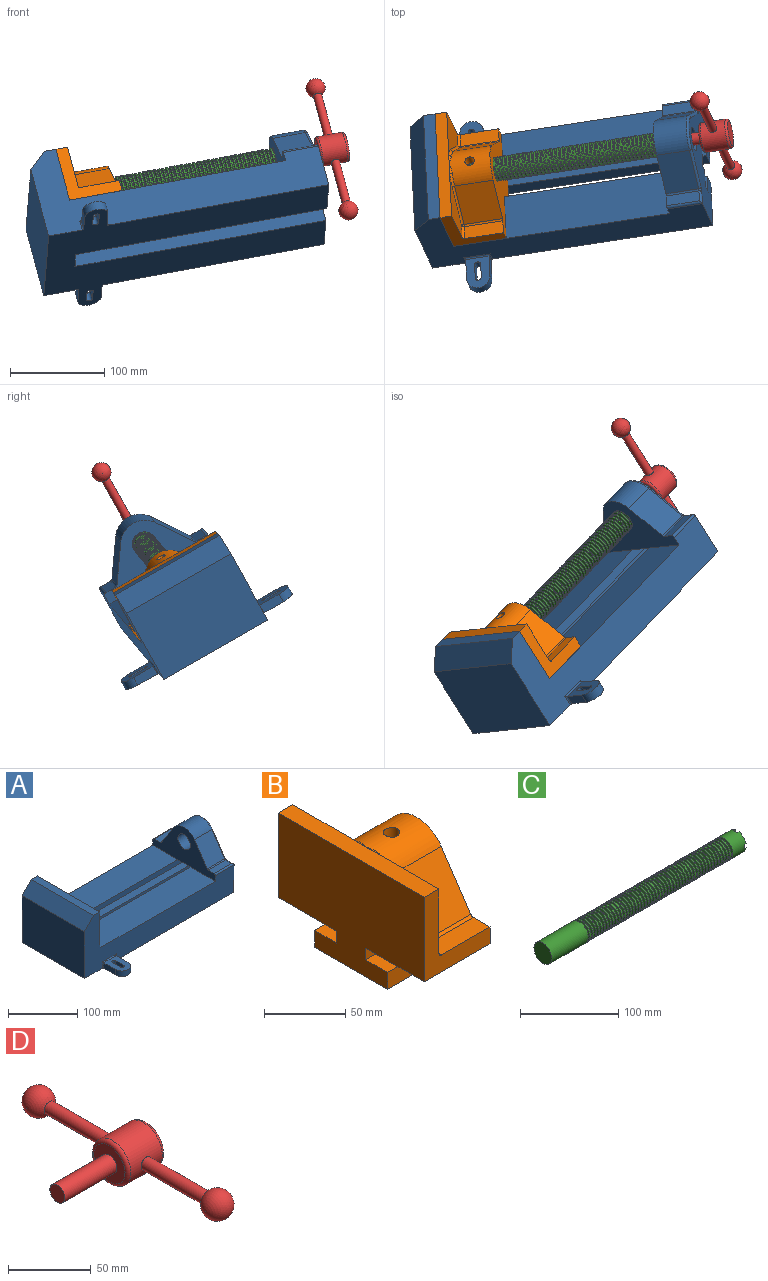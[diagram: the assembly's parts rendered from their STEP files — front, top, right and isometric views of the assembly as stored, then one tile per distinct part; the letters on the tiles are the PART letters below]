
ASSEMBLY  parts=4 mates=6
PART A: 61 faces, bbox 304.8x203.2x103.7 mm
  f0: plane 304.8x101.6mm, normal (0,1,0), area 13520.3mm2, adj f3,f4,f5,f6,f7,f8,f9,f16
  f1: plane 304.8x101.6mm, normal (0,-1,0), area 13520.3mm2, adj f2,f3,f5,f6,f7,f8,f9,f16
  f2: plane 234.95x50.8mm, normal (0,0,1), area 11935.5mm2, adj f1,f5,f16,f26
  f3: plane 127x99.06mm, normal (1,0,0), area 7097.5mm2, adj f0,f1,f9,f14,f17,f18,f19,f20
  f4: plane 234.95x50.8mm, normal (0,0,1), area 11935.5mm2, adj f0,f5,f16,f27
  f5: plane 127x101.6mm, normal (1,0,0), area 9516.1mm2, adj f0,f1,f2,f4,f6,f9,f18,f19
  f6: plane 127x12.7mm, normal (0,0,1), area 1612.9mm2, adj f0,f1,f5,f7
  f7: plane 127x19.05mm, normal (-0.71,0,0.71), area 3421.5mm2, adj f0,f1,f6,f8
  f8: plane 127x82.55mm, normal (-1,0,0), area 10483.8mm2, adj f0,f1,f7,f9
  f9: plane 304.8x203.2mm, normal (0,0,-1), area 33298.3mm2, adj f0,f1,f3,f5,f8,f21,f22,f39
  f10: plane 35.56x11.98mm, normal (0,0,1), area 426mm2, adj f16,f28,f29,f30
  f11: plane 38.43x35.56mm, normal (0,0.83,0.56), area 1645.4mm2, adj f12,f16,f29,f32
  f12: cylinder r=25.4mm len=42.19mm, axis (1,0,0), area 1770.2mm2, adj f11,f13,f16,f33
  f13: plane 38.43x35.56mm, normal (0,-0.83,0.56), area 1645.4mm2, adj f12,f16,f34,f35
  f14: cylinder r=12.7mm len=38.1mm, axis (1,0,0), area 3040.2mm2, adj f3,f16
  f15: plane 35.56x11.98mm, normal (0,0,1), area 426mm2, adj f16,f34,f36,f38
  f16: plane 127x63.5mm, normal (-1,0,0), area 4155.5mm2, adj f0,f1,f2,f4,f10,f11,f12,f13
  f17: plane 38.1x25.4mm, normal (0,0,-1), area 967.7mm2, adj f3,f16,f26,f27
  f18: plane 273.05x19.05mm, normal (0,0,-1), area 5201.6mm2, adj f3,f5,f19,f26
  f19: plane 273.05x12.7mm, normal (0,1,0), area 3467.7mm2, adj f3,f5,f18,f20
  f20: plane 273.05x19.05mm, normal (0,0,1), area 5201.6mm2, adj f3,f5,f19,f21
  f21: plane 273.05x16.51mm, normal (0,1,0), area 4508.1mm2, adj f3,f5,f9,f20
  f22: plane 273.05x16.51mm, normal (0,-1,0), area 4508.1mm2, adj f3,f5,f9,f23
  f23: plane 273.05x19.05mm, normal (0,0,1), area 5201.6mm2, adj f3,f5,f22,f24
  f24: plane 273.05x12.7mm, normal (0,-1,0), area 3467.7mm2, adj f3,f5,f23,f25
  f25: plane 273.05x19.05mm, normal (0,0,-1), area 5201.6mm2, adj f3,f5,f24,f27
  f26: plane 273.05x8.89mm, normal (0,1,0), area 2427.4mm2, adj f2,f3,f5,f17,f18
  f27: plane 273.05x8.89mm, normal (0,-1,0), area 2427.4mm2, adj f3,f4,f5,f17,f25
  f28: cylinder r=2.54mm len=38.1mm, axis (1,0,0), area 148.3mm2, adj f0,f10,f16,f30
  f29: cylinder r=2.54mm len=35.56mm, axis (-1,0,0), area 88.5mm2, adj f10,f11,f16,f31
  f30: cylinder r=2.54mm len=14.52mm, axis (0,1,0), area 54.3mm2, adj f3,f10,f28,f31
  f31: torus R=5.08mm, axis (-1,0,0), area 13.5mm2, adj f3,f29,f30,f32
  f32: cylinder r=2.54mm len=39.84mm, axis (0,0.56,-0.83), area 184.6mm2, adj f3,f11,f31,f33
  f33: torus R=22.86mm, axis (-1,0,0), area 191.4mm2, adj f3,f12,f32,f35
  f34: cylinder r=2.54mm len=35.56mm, axis (-1,0,0), area 88.5mm2, adj f13,f15,f16,f37
  f35: cylinder r=2.54mm len=39.84mm, axis (0,0.56,0.83), area 184.6mm2, adj f3,f13,f33,f37
  f36: cylinder r=2.54mm len=38.1mm, axis (-1,0,0), area 148.3mm2, adj f1,f15,f16,f38
  f37: torus R=5.08mm, axis (-1,0,0), area 13.5mm2, adj f3,f34,f35,f38
  f38: cylinder r=2.54mm len=14.52mm, axis (0,1,0), area 54.3mm2, adj f3,f15,f36,f37
  f39: plane 23.88x9.53mm, normal (-1,0,0), area 227.4mm2, adj f9,f45,f46,f60
  f40: plane 23.88x9.53mm, normal (1,0,0), area 227.4mm2, adj f9,f45,f46,f58
  f41: cylinder r=3.3mm len=9.53mm, axis (0,0,-1), area 98.8mm2, adj f9,f42,f44,f46
  f42: plane 15.62x9.53mm, normal (-1,0,0), area 148.8mm2, adj f9,f41,f43,f46
  f43: cylinder r=3.3mm len=9.53mm, axis (0,0,-1), area 98.8mm2, adj f9,f42,f44,f46
  f44: plane 15.62x9.53mm, normal (1,0,0), area 148.8mm2, adj f9,f41,f43,f46
  f45: cylinder r=12.7mm len=25.4mm, axis (0,0,-1), area 380mm2, adj f9,f39,f40,f46
  f46: plane 36.58x25.4mm, normal (0,0,1), area 722.4mm2, adj f39,f40,f41,f42,f43,f44,f45,f59
  f47: plane 23.88x9.53mm, normal (-1,0,0), area 227.4mm2, adj f9,f53,f54,f56
  f48: plane 23.88x9.53mm, normal (1,0,0), area 227.4mm2, adj f9,f53,f54,f55
  f49: cylinder r=3.3mm len=9.53mm, axis (0,0,-1), area 98.8mm2, adj f9,f50,f52,f54
  f50: plane 15.62x9.53mm, normal (-1,0,0), area 148.8mm2, adj f9,f49,f51,f54
  f51: cylinder r=3.3mm len=9.53mm, axis (0,0,-1), area 98.8mm2, adj f9,f50,f52,f54
  f52: plane 15.62x9.53mm, normal (1,0,0), area 148.8mm2, adj f9,f49,f51,f54
  f53: cylinder r=12.7mm len=25.4mm, axis (0,0,-1), area 380mm2, adj f9,f47,f48,f54
  f54: plane 36.58x25.4mm, normal (0,0,1), area 722.4mm2, adj f47,f48,f49,f50,f51,f52,f53,f57
  f55: cylinder r=1.52mm len=11.05mm, axis (0,0,-1), area 24.1mm2, adj f0,f9,f48,f57
  f56: cylinder r=1.52mm len=11.05mm, axis (0,0,1), area 24.1mm2, adj f0,f9,f47,f57
  f57: cylinder r=1.52mm len=28.45mm, axis (1,0,0), area 63.5mm2, adj f0,f54,f55,f56
  f58: cylinder r=1.52mm len=11.05mm, axis (0,0,1), area 24.1mm2, adj f1,f9,f40,f59
  f59: cylinder r=1.52mm len=28.45mm, axis (-1,0,0), area 63.5mm2, adj f1,f46,f58,f60
  f60: cylinder r=1.52mm len=11.05mm, axis (0,0,-1), area 24.1mm2, adj f1,f9,f39,f59
PART B: 36 faces, bbox 57.2x127x89 mm
  f0: plane 57.15x50.8mm, normal (0,0,-1), area 2903.2mm2, adj f6,f9,f10,f23
  f1: cylinder r=12.7mm len=44.45mm, axis (1,0,0), area 3464.3mm2, adj f6,f15,f16
  f2: plane 41.91x14.52mm, normal (0,0,1), area 608.5mm2, adj f6,f11,f24,f25
  f3: plane 51.86x48.26mm, normal (1,0,0), area 1495.7mm2, adj f8,f10,f31,f33,f35
  f4: plane 51.86x48.26mm, normal (1,0,0), area 1495.7mm2, adj f8,f11,f24,f28,f29
  f5: plane 57.15x50.8mm, normal (0,0,-1), area 2903.2mm2, adj f6,f9,f11,f22
  f6: plane 127x85.09mm, normal (1,0,0), area 5190.6mm2, adj f0,f1,f2,f5,f7,f10,f11,f12
  f7: plane 41.91x14.52mm, normal (0,0,1), area 608.5mm2, adj f6,f10,f30,f31
  f8: plane 127x12.7mm, normal (0,0,1), area 1612.9mm2, adj f3,f4,f9,f10,f11,f26,f34
  f9: plane 127x85.09mm, normal (-1,0,0), area 9096.8mm2, adj f0,f5,f8,f10,f11,f17,f18,f19
  f10: plane 63.5x57.15mm, normal (0,-1,0), area 1372.3mm2, adj f0,f3,f6,f7,f8,f9,f31
  f11: plane 63.5x57.15mm, normal (0,1,0), area 1372.3mm2, adj f2,f4,f5,f6,f8,f9,f24
  f12: plane 41.91x38.43mm, normal (0,-0.83,0.56), area 1939.2mm2, adj f6,f13,f30,f33
  f13: cylinder r=25.4mm len=44.45mm, axis (1,0,0), area 2026.5mm2, adj f6,f12,f14,f16,f26,f28,f34,f35
  f14: plane 41.91x38.43mm, normal (0,0.83,0.56), area 1939.2mm2, adj f6,f13,f25,f29
  f15: plane 25.4x25.4mm, normal (1,0,0), area 506.7mm2, adj f1
  f16: cylinder r=5.08mm len=13.76mm, axis (0,0,1), area 414mm2, adj f1,f13
  f17: plane 57.15x19.05mm, normal (0,0,1), area 1088.7mm2, adj f6,f9,f18,f23
  f18: plane 57.15x12.7mm, normal (0,-1,0), area 725.8mm2, adj f6,f9,f17,f19
  f19: plane 63.5x57.15mm, normal (0,0,-1), area 3629mm2, adj f6,f9,f18,f20
  f20: plane 57.15x12.7mm, normal (0,1,0), area 725.8mm2, adj f6,f9,f19,f21
  f21: plane 57.15x19.05mm, normal (0,0,1), area 1088.7mm2, adj f6,f9,f20,f22
  f22: plane 57.15x8.89mm, normal (0,1,0), area 508.1mm2, adj f5,f6,f9,f21
  f23: plane 57.15x8.89mm, normal (0,-1,0), area 508.1mm2, adj f0,f6,f9,f17
  f24: cylinder r=2.54mm len=14.52mm, axis (0,-1,0), area 57.9mm2, adj f2,f4,f11,f27
  f25: cylinder r=2.54mm len=41.91mm, axis (1,0,0), area 104.3mm2, adj f2,f6,f14,f27
  f26: bspline ~12.24x2.8mm, area 20.9mm2, adj f8,f13,f28
  f27: sphere r=2.54mm, area 6.3mm2, adj f24,f25,f29
  f28: torus R=27.94mm, axis (1,0,0), area 57.8mm2, adj f4,f13,f26,f29
  f29: cylinder r=2.54mm len=39.84mm, axis (0,-0.56,0.83), area 184.6mm2, adj f4,f14,f27,f28
  f30: cylinder r=2.54mm len=41.91mm, axis (1,0,0), area 104.3mm2, adj f6,f7,f12,f32
  f31: cylinder r=2.54mm len=14.52mm, axis (0,-1,0), area 57.9mm2, adj f3,f7,f10,f32
  f32: sphere r=2.54mm, area 6.3mm2, adj f30,f31,f33
  f33: cylinder r=2.54mm len=39.84mm, axis (0,-0.56,-0.83), area 184.6mm2, adj f3,f12,f32,f35
  f34: bspline ~12.24x2.8mm, area 20.9mm2, adj f8,f13,f35
  f35: torus R=27.94mm, axis (1,0,0), area 57.8mm2, adj f3,f13,f33,f34
PART C: 220 faces, bbox 279.4x25.4x25.4 mm
  f0: cylinder r=12.7mm len=25.4mm, axis (-1,0,0), area 1468.2mm2, adj f1,f2,f3,f5,f7,f208,f209,f210
  f1: plane 9.9x9.9mm, normal (1,0,0), area 62.3mm2, adj f0,f4,f213,f216
  f2: plane 9.9x9.9mm, normal (1,0,0), area 62.3mm2, adj f0,f4,f210,f218
  f3: plane 9.9x9.9mm, normal (1,0,0), area 62.3mm2, adj f0,f4,f209,f212
  f4: cylinder r=6.35mm len=25.4mm, axis (1,0,0), area 960.3mm2, adj f1,f2,f3,f5,f6,f208,f209,f210
  f5: plane 9.9x9.9mm, normal (1,0,0), area 62.3mm2, adj f0,f4,f215,f217
  f6: plane 12.7x12.7mm, normal (1,0,0), area 126.7mm2, adj f4
  f7: cone r=12.7mm half-angle=76deg, axis (1,0,0), area 188mm2, adj f0,f9
  f8: cone r=10.16mm half-angle=76deg, axis (-1,0,0), area 188mm2, adj f9,f10
  f9: cylinder r=10.16mm len=20.32mm, axis (1,0,0), area 81.1mm2, adj f7,f8
  f10: cylinder r=12.7mm len=25.4mm, axis (-1,0,0), area 131.7mm2, adj f8,f11
  f11: cone r=12.7mm half-angle=76deg, axis (1,0,0), area 188mm2, adj f10,f13
  f12: cone r=10.16mm half-angle=76deg, axis (-1,0,0), area 188mm2, adj f13,f14
  f13: cylinder r=10.16mm len=20.32mm, axis (1,0,0), area 81.1mm2, adj f11,f12
  f14: cylinder r=12.7mm len=25.4mm, axis (-1,0,0), area 131.7mm2, adj f12,f15
  f15: cone r=12.7mm half-angle=76deg, axis (1,0,0), area 188mm2, adj f14,f17
  f16: cone r=10.16mm half-angle=76deg, axis (-1,0,0), area 188mm2, adj f17,f18
  f17: cylinder r=10.16mm len=20.32mm, axis (1,0,0), area 81.1mm2, adj f15,f16
  f18: cylinder r=12.7mm len=25.4mm, axis (-1,0,0), area 131.7mm2, adj f16,f19
  f19: cone r=12.7mm half-angle=76deg, axis (1,0,0), area 188mm2, adj f18,f21
  f20: cone r=10.16mm half-angle=76deg, axis (-1,0,0), area 188mm2, adj f21,f22
  f21: cylinder r=10.16mm len=20.32mm, axis (1,0,0), area 81.1mm2, adj f19,f20
  f22: cylinder r=12.7mm len=25.4mm, axis (-1,0,0), area 131.7mm2, adj f20,f23
  f23: cone r=12.7mm half-angle=76deg, axis (1,0,0), area 188mm2, adj f22,f25
  f24: cone r=10.16mm half-angle=76deg, axis (-1,0,0), area 188mm2, adj f25,f26
  f25: cylinder r=10.16mm len=20.32mm, axis (1,0,0), area 81.1mm2, adj f23,f24
  f26: cylinder r=12.7mm len=25.4mm, axis (-1,0,0), area 131.7mm2, adj f24,f27
  f27: cone r=12.7mm half-angle=76deg, axis (1,0,0), area 188mm2, adj f26,f29
  f28: cone r=10.16mm half-angle=76deg, axis (-1,0,0), area 188mm2, adj f29,f30
  f29: cylinder r=10.16mm len=20.32mm, axis (1,0,0), area 81.1mm2, adj f27,f28
  f30: cylinder r=12.7mm len=25.4mm, axis (-1,0,0), area 131.7mm2, adj f28,f31
  f31: cone r=12.7mm half-angle=76deg, axis (1,0,0), area 188mm2, adj f30,f33
  f32: cone r=10.16mm half-angle=76deg, axis (-1,0,0), area 188mm2, adj f33,f34
  f33: cylinder r=10.16mm len=20.32mm, axis (1,0,0), area 81.1mm2, adj f31,f32
  f34: cylinder r=12.7mm len=25.4mm, axis (-1,0,0), area 131.7mm2, adj f32,f35
  f35: cone r=12.7mm half-angle=76deg, axis (1,0,0), area 188mm2, adj f34,f37
  f36: cone r=10.16mm half-angle=76deg, axis (-1,0,0), area 188mm2, adj f37,f38
  f37: cylinder r=10.16mm len=20.32mm, axis (1,0,0), area 81.1mm2, adj f35,f36
  f38: cylinder r=12.7mm len=25.4mm, axis (-1,0,0), area 131.7mm2, adj f36,f39
  f39: cone r=12.7mm half-angle=76deg, axis (1,0,0), area 188mm2, adj f38,f41
  f40: cone r=10.16mm half-angle=76deg, axis (-1,0,0), area 188mm2, adj f41,f42
  f41: cylinder r=10.16mm len=20.32mm, axis (1,0,0), area 81.1mm2, adj f39,f40
  f42: cylinder r=12.7mm len=25.4mm, axis (-1,0,0), area 131.7mm2, adj f40,f43
  f43: cone r=12.7mm half-angle=76deg, axis (1,0,0), area 188mm2, adj f42,f45
  f44: cone r=10.16mm half-angle=76deg, axis (-1,0,0), area 188mm2, adj f45,f46
  f45: cylinder r=10.16mm len=20.32mm, axis (1,0,0), area 81.1mm2, adj f43,f44
  f46: cylinder r=12.7mm len=25.4mm, axis (-1,0,0), area 131.7mm2, adj f44,f47
  f47: cone r=12.7mm half-angle=76deg, axis (1,0,0), area 188mm2, adj f46,f49
  f48: cone r=10.16mm half-angle=76deg, axis (-1,0,0), area 188mm2, adj f49,f50
  f49: cylinder r=10.16mm len=20.32mm, axis (1,0,0), area 81.1mm2, adj f47,f48
  f50: cylinder r=12.7mm len=25.4mm, axis (-1,0,0), area 131.7mm2, adj f48,f51
  f51: cone r=12.7mm half-angle=76deg, axis (1,0,0), area 188mm2, adj f50,f53
  f52: cone r=10.16mm half-angle=76deg, axis (-1,0,0), area 188mm2, adj f53,f54
  f53: cylinder r=10.16mm len=20.32mm, axis (1,0,0), area 81.1mm2, adj f51,f52
  f54: cylinder r=12.7mm len=25.4mm, axis (-1,0,0), area 131.7mm2, adj f52,f55
  f55: cone r=12.7mm half-angle=76deg, axis (1,0,0), area 188mm2, adj f54,f57
  f56: cone r=10.16mm half-angle=76deg, axis (-1,0,0), area 188mm2, adj f57,f58
  f57: cylinder r=10.16mm len=20.32mm, axis (1,0,0), area 81.1mm2, adj f55,f56
  f58: cylinder r=12.7mm len=25.4mm, axis (-1,0,0), area 131.7mm2, adj f56,f59
  f59: cone r=12.7mm half-angle=76deg, axis (1,0,0), area 188mm2, adj f58,f61
  f60: cone r=10.16mm half-angle=76deg, axis (-1,0,0), area 188mm2, adj f61,f62
  f61: cylinder r=10.16mm len=20.32mm, axis (1,0,0), area 81.1mm2, adj f59,f60
  f62: cylinder r=12.7mm len=25.4mm, axis (-1,0,0), area 131.7mm2, adj f60,f63
  f63: cone r=12.7mm half-angle=76deg, axis (1,0,0), area 188mm2, adj f62,f65
  f64: cone r=10.16mm half-angle=76deg, axis (-1,0,0), area 188mm2, adj f65,f66
  f65: cylinder r=10.16mm len=20.32mm, axis (1,0,0), area 81.1mm2, adj f63,f64
  f66: cylinder r=12.7mm len=25.4mm, axis (-1,0,0), area 131.7mm2, adj f64,f67
  f67: cone r=12.7mm half-angle=76deg, axis (1,0,0), area 188mm2, adj f66,f69
  f68: cone r=10.16mm half-angle=76deg, axis (-1,0,0), area 188mm2, adj f69,f70
  f69: cylinder r=10.16mm len=20.32mm, axis (1,0,0), area 81.1mm2, adj f67,f68
  f70: cylinder r=12.7mm len=25.4mm, axis (-1,0,0), area 131.7mm2, adj f68,f71
  f71: cone r=12.7mm half-angle=76deg, axis (1,0,0), area 188mm2, adj f70,f73
  f72: cone r=10.16mm half-angle=76deg, axis (-1,0,0), area 188mm2, adj f73,f74
  f73: cylinder r=10.16mm len=20.32mm, axis (1,0,0), area 81.1mm2, adj f71,f72
  f74: cylinder r=12.7mm len=25.4mm, axis (-1,0,0), area 131.7mm2, adj f72,f75
  f75: cone r=12.7mm half-angle=76deg, axis (1,0,0), area 188mm2, adj f74,f77
  f76: cone r=10.16mm half-angle=76deg, axis (-1,0,0), area 188mm2, adj f77,f78
  f77: cylinder r=10.16mm len=20.32mm, axis (1,0,0), area 81.1mm2, adj f75,f76
  f78: cylinder r=12.7mm len=25.4mm, axis (-1,0,0), area 131.7mm2, adj f76,f79
  f79: cone r=12.7mm half-angle=76deg, axis (1,0,0), area 188mm2, adj f78,f81
  f80: cone r=10.16mm half-angle=76deg, axis (-1,0,0), area 188mm2, adj f81,f82
  f81: cylinder r=10.16mm len=20.32mm, axis (1,0,0), area 81.1mm2, adj f79,f80
  f82: cylinder r=12.7mm len=25.4mm, axis (-1,0,0), area 131.7mm2, adj f80,f83
  f83: cone r=12.7mm half-angle=76deg, axis (1,0,0), area 188mm2, adj f82,f85
  f84: cone r=10.16mm half-angle=76deg, axis (-1,0,0), area 188mm2, adj f85,f86
  f85: cylinder r=10.16mm len=20.32mm, axis (1,0,0), area 81.1mm2, adj f83,f84
  f86: cylinder r=12.7mm len=25.4mm, axis (-1,0,0), area 131.7mm2, adj f84,f87
  f87: cone r=12.7mm half-angle=76deg, axis (1,0,0), area 188mm2, adj f86,f89
  f88: cone r=10.16mm half-angle=76deg, axis (-1,0,0), area 188mm2, adj f89,f90
  f89: cylinder r=10.16mm len=20.32mm, axis (1,0,0), area 81.1mm2, adj f87,f88
  f90: cylinder r=12.7mm len=25.4mm, axis (-1,0,0), area 131.7mm2, adj f88,f91
  f91: cone r=12.7mm half-angle=76deg, axis (1,0,0), area 188mm2, adj f90,f93
  f92: cone r=10.16mm half-angle=76deg, axis (-1,0,0), area 188mm2, adj f93,f94
  f93: cylinder r=10.16mm len=20.32mm, axis (1,0,0), area 81.1mm2, adj f91,f92
  f94: cylinder r=12.7mm len=25.4mm, axis (-1,0,0), area 131.7mm2, adj f92,f95
  f95: cone r=12.7mm half-angle=76deg, axis (1,0,0), area 188mm2, adj f94,f97
  f96: cone r=10.16mm half-angle=76deg, axis (-1,0,0), area 188mm2, adj f97,f98
  f97: cylinder r=10.16mm len=20.32mm, axis (1,0,0), area 81.1mm2, adj f95,f96
  f98: cylinder r=12.7mm len=25.4mm, axis (-1,0,0), area 131.7mm2, adj f96,f99
  f99: cone r=12.7mm half-angle=76deg, axis (1,0,0), area 188mm2, adj f98,f101
  f100: cone r=10.16mm half-angle=76deg, axis (-1,0,0), area 188mm2, adj f101,f102
  f101: cylinder r=10.16mm len=20.32mm, axis (1,0,0), area 81.1mm2, adj f99,f100
  f102: cylinder r=12.7mm len=25.4mm, axis (-1,0,0), area 131.7mm2, adj f100,f103
  f103: cone r=12.7mm half-angle=76deg, axis (1,0,0), area 188mm2, adj f102,f105
  f104: cone r=10.16mm half-angle=76deg, axis (-1,0,0), area 188mm2, adj f105,f106
  f105: cylinder r=10.16mm len=20.32mm, axis (1,0,0), area 81.1mm2, adj f103,f104
  f106: cylinder r=12.7mm len=25.4mm, axis (-1,0,0), area 131.7mm2, adj f104,f107
  f107: cone r=12.7mm half-angle=76deg, axis (1,0,0), area 188mm2, adj f106,f109
  f108: cone r=10.16mm half-angle=76deg, axis (-1,0,0), area 188mm2, adj f109,f110
  f109: cylinder r=10.16mm len=20.32mm, axis (1,0,0), area 81.1mm2, adj f107,f108
  f110: cylinder r=12.7mm len=25.4mm, axis (-1,0,0), area 131.7mm2, adj f108,f111
  f111: cone r=12.7mm half-angle=76deg, axis (1,0,0), area 188mm2, adj f110,f113
  f112: cone r=10.16mm half-angle=76deg, axis (-1,0,0), area 188mm2, adj f113,f114
  f113: cylinder r=10.16mm len=20.32mm, axis (1,0,0), area 81.1mm2, adj f111,f112
  f114: cylinder r=12.7mm len=25.4mm, axis (-1,0,0), area 131.7mm2, adj f112,f115
  f115: cone r=12.7mm half-angle=76deg, axis (1,0,0), area 188mm2, adj f114,f117
  f116: cone r=10.16mm half-angle=76deg, axis (-1,0,0), area 188mm2, adj f117,f118
  f117: cylinder r=10.16mm len=20.32mm, axis (1,0,0), area 81.1mm2, adj f115,f116
  f118: cylinder r=12.7mm len=25.4mm, axis (-1,0,0), area 131.7mm2, adj f116,f119
  f119: cone r=12.7mm half-angle=76deg, axis (1,0,0), area 188mm2, adj f118,f121
  f120: cone r=10.16mm half-angle=76deg, axis (-1,0,0), area 188mm2, adj f121,f122
  f121: cylinder r=10.16mm len=20.32mm, axis (1,0,0), area 81.1mm2, adj f119,f120
  f122: cylinder r=12.7mm len=25.4mm, axis (-1,0,0), area 131.7mm2, adj f120,f123
  f123: cone r=12.7mm half-angle=76deg, axis (1,0,0), area 188mm2, adj f122,f125
  f124: cone r=10.16mm half-angle=76deg, axis (-1,0,0), area 188mm2, adj f125,f126
  f125: cylinder r=10.16mm len=20.32mm, axis (1,0,0), area 81.1mm2, adj f123,f124
  f126: cylinder r=12.7mm len=25.4mm, axis (-1,0,0), area 131.7mm2, adj f124,f127
  f127: cone r=12.7mm half-angle=76deg, axis (1,0,0), area 188mm2, adj f126,f129
  f128: cone r=10.16mm half-angle=76deg, axis (-1,0,0), area 188mm2, adj f129,f130
  f129: cylinder r=10.16mm len=20.32mm, axis (1,0,0), area 81.1mm2, adj f127,f128
  f130: cylinder r=12.7mm len=25.4mm, axis (-1,0,0), area 131.7mm2, adj f128,f131
  f131: cone r=12.7mm half-angle=76deg, axis (1,0,0), area 188mm2, adj f130,f133
  f132: cone r=10.16mm half-angle=76deg, axis (-1,0,0), area 188mm2, adj f133,f134
  f133: cylinder r=10.16mm len=20.32mm, axis (1,0,0), area 81.1mm2, adj f131,f132
  f134: cylinder r=12.7mm len=25.4mm, axis (-1,0,0), area 131.7mm2, adj f132,f135
  f135: cone r=12.7mm half-angle=76deg, axis (1,0,0), area 188mm2, adj f134,f137
  f136: cone r=10.16mm half-angle=76deg, axis (-1,0,0), area 188mm2, adj f137,f138
  f137: cylinder r=10.16mm len=20.32mm, axis (1,0,0), area 81.1mm2, adj f135,f136
  f138: cylinder r=12.7mm len=25.4mm, axis (-1,0,0), area 131.7mm2, adj f136,f139
  f139: cone r=12.7mm half-angle=76deg, axis (1,0,0), area 188mm2, adj f138,f141
  f140: cone r=10.16mm half-angle=76deg, axis (-1,0,0), area 188mm2, adj f141,f142
  f141: cylinder r=10.16mm len=20.32mm, axis (1,0,0), area 81.1mm2, adj f139,f140
  f142: cylinder r=12.7mm len=25.4mm, axis (-1,0,0), area 131.7mm2, adj f140,f143
  f143: cone r=12.7mm half-angle=76deg, axis (1,0,0), area 188mm2, adj f142,f145
  f144: cone r=10.16mm half-angle=76deg, axis (-1,0,0), area 188mm2, adj f145,f146
  f145: cylinder r=10.16mm len=20.32mm, axis (1,0,0), area 81.1mm2, adj f143,f144
  f146: cylinder r=12.7mm len=25.4mm, axis (-1,0,0), area 131.7mm2, adj f144,f147
  f147: cone r=12.7mm half-angle=76deg, axis (1,0,0), area 188mm2, adj f146,f149
  f148: cone r=10.16mm half-angle=76deg, axis (-1,0,0), area 188mm2, adj f149,f150
  f149: cylinder r=10.16mm len=20.32mm, axis (1,0,0), area 81.1mm2, adj f147,f148
  f150: cylinder r=12.7mm len=25.4mm, axis (-1,0,0), area 131.7mm2, adj f148,f151
  f151: cone r=12.7mm half-angle=76deg, axis (1,0,0), area 188mm2, adj f150,f153
  f152: cone r=10.16mm half-angle=76deg, axis (-1,0,0), area 188mm2, adj f153,f154
  f153: cylinder r=10.16mm len=20.32mm, axis (1,0,0), area 81.1mm2, adj f151,f152
  f154: cylinder r=12.7mm len=25.4mm, axis (-1,0,0), area 131.7mm2, adj f152,f155
  f155: cone r=12.7mm half-angle=76deg, axis (1,0,0), area 188mm2, adj f154,f157
  f156: cone r=10.16mm half-angle=76deg, axis (-1,0,0), area 188mm2, adj f157,f158
  f157: cylinder r=10.16mm len=20.32mm, axis (1,0,0), area 81.1mm2, adj f155,f156
  f158: cylinder r=12.7mm len=25.4mm, axis (-1,0,0), area 131.7mm2, adj f156,f159
  f159: cone r=12.7mm half-angle=76deg, axis (1,0,0), area 188mm2, adj f158,f161
  f160: cone r=10.16mm half-angle=76deg, axis (-1,0,0), area 188mm2, adj f161,f162
  f161: cylinder r=10.16mm len=20.32mm, axis (1,0,0), area 81.1mm2, adj f159,f160
  f162: cylinder r=12.7mm len=25.4mm, axis (-1,0,0), area 131.7mm2, adj f160,f163
  f163: cone r=12.7mm half-angle=76deg, axis (1,0,0), area 188mm2, adj f162,f165
  f164: cone r=10.16mm half-angle=76deg, axis (-1,0,0), area 188mm2, adj f165,f166
  f165: cylinder r=10.16mm len=20.32mm, axis (1,0,0), area 81.1mm2, adj f163,f164
  f166: cylinder r=12.7mm len=25.4mm, axis (-1,0,0), area 131.7mm2, adj f164,f167
  f167: cone r=12.7mm half-angle=76deg, axis (1,0,0), area 188mm2, adj f166,f169
  f168: cone r=10.16mm half-angle=76deg, axis (-1,0,0), area 188mm2, adj f169,f170
  f169: cylinder r=10.16mm len=20.32mm, axis (1,0,0), area 81.1mm2, adj f167,f168
  f170: cylinder r=12.7mm len=25.4mm, axis (-1,0,0), area 131.7mm2, adj f168,f171
  f171: cone r=12.7mm half-angle=76deg, axis (1,0,0), area 188mm2, adj f170,f173
  f172: cone r=10.16mm half-angle=76deg, axis (-1,0,0), area 188mm2, adj f173,f174
  f173: cylinder r=10.16mm len=20.32mm, axis (1,0,0), area 81.1mm2, adj f171,f172
  f174: cylinder r=12.7mm len=25.4mm, axis (-1,0,0), area 131.7mm2, adj f172,f175
  f175: cone r=12.7mm half-angle=76deg, axis (1,0,0), area 188mm2, adj f174,f177
  f176: cone r=10.16mm half-angle=76deg, axis (-1,0,0), area 188mm2, adj f177,f178
  f177: cylinder r=10.16mm len=20.32mm, axis (1,0,0), area 81.1mm2, adj f175,f176
  f178: cylinder r=12.7mm len=25.4mm, axis (-1,0,0), area 131.7mm2, adj f176,f179
  f179: cone r=12.7mm half-angle=76deg, axis (1,0,0), area 188mm2, adj f178,f181
  f180: cone r=10.16mm half-angle=76deg, axis (-1,0,0), area 188mm2, adj f181,f182
  f181: cylinder r=10.16mm len=20.32mm, axis (1,0,0), area 81.1mm2, adj f179,f180
  f182: cylinder r=12.7mm len=25.4mm, axis (-1,0,0), area 131.7mm2, adj f180,f183
  f183: cone r=12.7mm half-angle=76deg, axis (1,0,0), area 188mm2, adj f182,f185
  f184: cone r=10.16mm half-angle=76deg, axis (-1,0,0), area 188mm2, adj f185,f186
  f185: cylinder r=10.16mm len=20.32mm, axis (1,0,0), area 81.1mm2, adj f183,f184
  f186: cylinder r=12.7mm len=25.4mm, axis (-1,0,0), area 131.7mm2, adj f184,f187
  f187: cone r=12.7mm half-angle=76deg, axis (1,0,0), area 188mm2, adj f186,f189
  f188: cone r=10.16mm half-angle=76deg, axis (-1,0,0), area 188mm2, adj f189,f190
  f189: cylinder r=10.16mm len=20.32mm, axis (1,0,0), area 81.1mm2, adj f187,f188
  f190: cylinder r=12.7mm len=25.4mm, axis (-1,0,0), area 131.7mm2, adj f188,f191
  f191: cone r=12.7mm half-angle=76deg, axis (1,0,0), area 188mm2, adj f190,f193
  f192: cone r=10.16mm half-angle=76deg, axis (-1,0,0), area 188mm2, adj f193,f194
  f193: cylinder r=10.16mm len=20.32mm, axis (1,0,0), area 81.1mm2, adj f191,f192
  f194: cylinder r=12.7mm len=25.4mm, axis (-1,0,0), area 131.7mm2, adj f192,f195
  f195: cone r=12.7mm half-angle=76deg, axis (1,0,0), area 188mm2, adj f194,f197
  f196: cone r=10.16mm half-angle=76deg, axis (-1,0,0), area 188mm2, adj f197,f198
  f197: cylinder r=10.16mm len=20.32mm, axis (1,0,0), area 81.1mm2, adj f195,f196
  f198: cylinder r=12.7mm len=25.4mm, axis (-1,0,0), area 131.7mm2, adj f196,f199
  f199: cone r=12.7mm half-angle=76deg, axis (1,0,0), area 188mm2, adj f198,f201
  f200: cone r=10.16mm half-angle=76deg, axis (-1,0,0), area 188mm2, adj f201,f202
  f201: cylinder r=10.16mm len=20.32mm, axis (1,0,0), area 81.1mm2, adj f199,f200
  f202: cylinder r=12.7mm len=25.4mm, axis (-1,0,0), area 131.7mm2, adj f200,f203
  f203: cone r=12.7mm half-angle=76deg, axis (1,0,0), area 188mm2, adj f202,f205
  f204: cone r=10.16mm half-angle=76deg, axis (-1,0,0), area 188mm2, adj f205,f207
  f205: cylinder r=10.16mm len=20.32mm, axis (1,0,0), area 81.1mm2, adj f203,f204
  f206: plane 25.4x25.4mm, normal (-1,0,0), area 506.7mm2, adj f207
  f207: cylinder r=12.7mm len=52.45mm, axis (-1,0,0), area 4185.4mm2, adj f204,f206
  f208: plane 6.88x5.08mm, normal (1,0,0), area 32.7mm2, adj f0,f4,f209,f210
  f209: plane 6.62x2.54mm, normal (0,-1,0), area 16.8mm2, adj f0,f3,f4,f208
  f210: plane 6.62x2.54mm, normal (0,1,0), area 16.8mm2, adj f0,f2,f4,f208
  f211: plane 6.88x5.08mm, normal (1,0,0), area 32.7mm2, adj f0,f4,f212,f213
  f212: plane 6.62x2.54mm, normal (0,0,1), area 16.8mm2, adj f0,f3,f4,f211
  f213: plane 6.62x2.54mm, normal (0,0,-1), area 16.8mm2, adj f0,f1,f4,f211
  f214: plane 6.88x5.08mm, normal (1,0,0), area 32.7mm2, adj f0,f4,f215,f216
  f215: plane 6.62x2.54mm, normal (0,1,0), area 16.8mm2, adj f0,f4,f5,f214
  f216: plane 6.62x2.54mm, normal (0,-1,0), area 16.8mm2, adj f0,f1,f4,f214
  f217: plane 6.62x2.54mm, normal (0,0,-1), area 16.8mm2, adj f0,f4,f5,f219
  f218: plane 6.62x2.54mm, normal (0,0,1), area 16.8mm2, adj f0,f2,f4,f219
  f219: plane 6.88x5.08mm, normal (1,0,0), area 32.7mm2, adj f0,f4,f217,f218
PART D: 11 faces, bbox 76.2x172.7x34.4 mm
  f0: sphere r=10.16mm, area 1231.8mm2, adj f1
  f1: cylinder r=4.45mm len=51.82mm, axis (0,1,0), area 1438.5mm2, adj f0,f4
  f2: sphere r=10.16mm, area 1231.8mm2, adj f3
  f3: cylinder r=4.45mm len=51.82mm, axis (0,1,0), area 1438.5mm2, adj f2,f4
  f4: cylinder r=15.88mm len=31.75mm, axis (-1,0,0), area 2534.7mm2, adj f1,f3,f9,f10
  f5: cylinder r=6.35mm len=44.45mm, axis (-1,0,0), area 1773.5mm2, adj f6,f8
  f6: plane 12.7x12.7mm, normal (-1,0,0), area 126.7mm2, adj f5
  f7: plane 26.67x26.67mm, normal (1,0,0), area 558.6mm2, adj f10
  f8: plane 26.67x26.67mm, normal (-1,0,0), area 432mm2, adj f5,f9
  f9: torus R=13.33mm, axis (1,0,0), area 374.8mm2, adj f4,f8
  f10: torus R=13.33mm, axis (1,0,0), area 374.8mm2, adj f4,f7
PLACE A rot(axis=(-0.91,-0.38,0.18),32.4deg) t=(56.44,33.34,2.23)mm
PLACE B rot(axis=(-0.91,-0.38,0.18),32.4deg) t=(56.44,33.34,2.23)mm
PLACE C rot(axis=(-0.99,-0.13,-0.05),120deg) t=(9.88,-1.32,98.89)mm
PLACE D rot(axis=(-0.99,-0.13,-0.05),120deg) t=(12.97,-0.85,99.45)mm
MATE slider B.f9 <-> A.f5  axis (-0.97,-0.15,-0.18) through (-220.43,66.19,-45.74)mm
MATE revolute B.f28 <-> B.f6  axis (0.97,0.15,0.18) through (-170.97,37.74,28.38)mm
MATE ball B.f28 <-> C.f7  axis (0.97,0.15,0.18) through (-170.97,37.74,28.38)mm
MATE revolute C.f7 <-> B.f28  axis (-0.97,-0.15,-0.18) through (-246.45,26.28,14.52)mm
MATE cylindrical B.f28 <-> B.f28  axis (0.97,0.15,0.18) through (-214.47,31.13,20.39)mm
MATE fastened D.f5 <-> C.f4  axis (-0.97,-0.15,-0.18) through (25.34,67.55,64.42)mm
